# Revit family: Franke_A400_FM_CM_FW(EU)
name_source: partatom
category: Specialty Equipment
revit_build: Autodesk Revit 2015 (Build: 20140606_1530(x64)
units: mm (PartAtom-declared; Revit-internal decimal feet)

## types (2) — shared parameters
Assembly Code = fully automatic coffee machine
Cycle (A400) = 50 Hz
Cycle (SU05) = 50 Hz
Cycle alternativ (A400) = 60 Hz
Cycle alternativ (SU05) = 60 Hz
Depth (mm) = 600 mm
Description = A400 fully automatic coffee machine incl. Refrigerator SU05 FM
Energy loss acc. to DIN 18873 (A400 FM incl. SU05 FM) = /
Height (mm) = 744 mm  [stored 2.44094 ft]
Incoming water (cold water) = 8 mm  [stored 0.0262467 ft]
Keynote = fully automatic coffee machine
Manufacturer = Franke
Max Overcurrent Protection (A400) = 16 A
Max Overcurrent Protection (SU05) = 16 A
Milk storage (SU05) = 5 l
Model = A400 FM CM FW
Noise emission = 70 dB
Number of Nutral Conductors (A400) = 1
Number of Nutral Conductors (SU05) = 1
Number of Poles (A400) = 1
Number of Poles (SU05) = 1
Number of Protective Conductors (A400) = 1
Number of Protective Conductors (SU05) = 1
Temperature range = 3° - 8°
URL = https://www.franke.com
Volts max. (A400) = 240 V
Volts max. (SU05) = 240 V
Volts min. (A400) = 220 V
Volts min. (SU05) = 220 V
Wastewater = 9 mm  [stored 0.0295276 ft]
Water pressure = 800000.0 Pa
Water pressure (with filter) = 600000.0 Pa
Watts max. (A400) = 2800 W
Watts max. (SU05) = 2300 W
Watts min. (A400) = 2400 W
Watts min. (SU05) = 1950 W
Weight = 64 kg
Width (mm) = 613 mm  [stored 2.01115 ft]
zero-valued in all types: Cost

## per-type parameters (varying)
| type | Frontcover |
| A400 FM CM FW(220-240V/anthracite/EU) | Franke Anthracite |
| A400 FM CM FW(220-240V/black line/EU) | Franke Black |

note: [stored X ft] marks values corroborated as IEEE doubles in the binary element streams (Revit-internal decimal feet)

## geometry (parser evidence)
native form markers: Extrusion x1
no freeform markers — native parametric forms only
